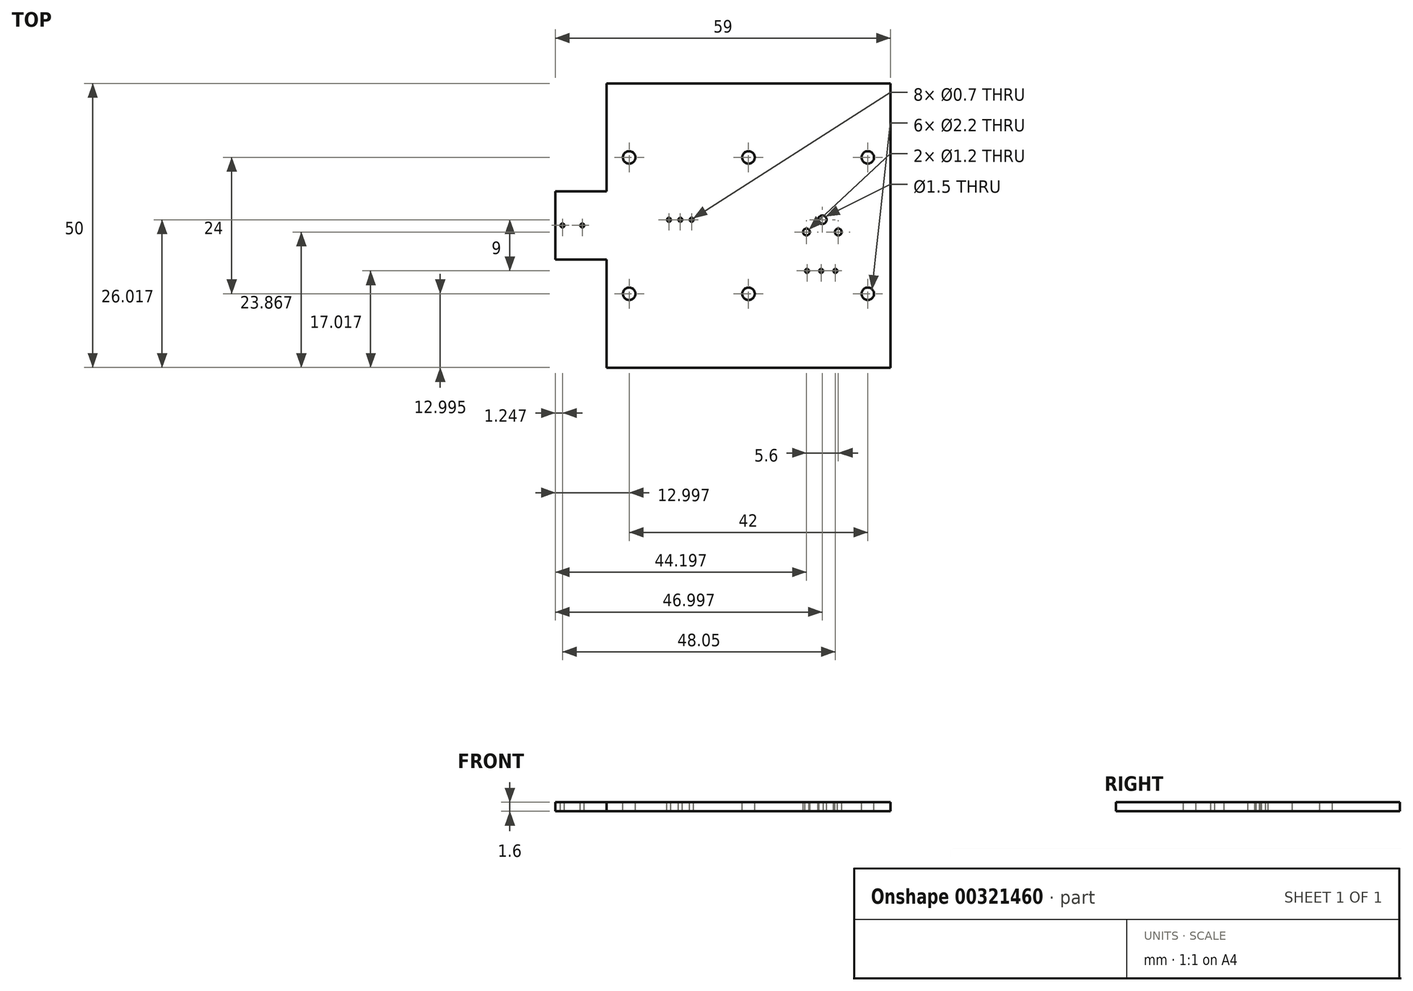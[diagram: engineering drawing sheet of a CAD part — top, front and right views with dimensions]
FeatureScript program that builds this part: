
annotation { "Feature Type Name" : "Feature", "Feature Type Description" : "" }
export const myFeature = defineFeature(function(context is Context, id is Id, definition is map)
    precondition{}
    {
        {
            var Q0;
            Q0=qCreatedBy(makeId("Top.planeOp"),FACE);
            var sketch = newSketch(context, id + "F0", { "sketchPlane" : qUnion([Q0])});
            skLineSegment(sketch, "E0", {"start": v(41.32, 33.18) * mm, "end": v(41.32, -3.82) * mm, "construction": true});
            skLineSegment(sketch, "E1.bottom", {"start": v(7.32, 8.68) * mm, "end": v(66.32, 8.68) * mm});
            skLineSegment(sketch, "E1.top", {"start": v(7.32, 20.68) * mm, "end": v(66.32, 20.68) * mm});
            skLineSegment(sketch, "E1.left", {"start": v(7.32, 8.68) * mm, "end": v(7.32, 20.68) * mm});
            skLineSegment(sketch, "E1.right", {"start": v(75.32, 8.68) * mm, "end": v(75.32, 20.68) * mm, "construction": true});
            skPoint(sketch, "E1.middle", {"position": v(41.32, 14.68) * mm});
            skLineSegment(sketch, "E2.bottom", {"start": v(66.32, 39.68) * mm, "end": v(16.32, 39.68) * mm});
            skLineSegment(sketch, "E2.top", {"start": v(66.32, -10.32) * mm, "end": v(16.32, -10.32) * mm});
            skLineSegment(sketch, "E2.left", {"start": v(66.32, 39.68) * mm, "end": v(66.32, -10.32) * mm});
            skLineSegment(sketch, "E2.right", {"start": v(16.32, 39.68) * mm, "end": v(16.32, -10.32) * mm});
            skSolve(sketch);
        }
        {
            var Q0;
            Q0 = qSketchRegion(id + "F0", true);
            extrude(context, id + "F1", {"entities" : qUnion([Q0]), "depth" : 1.6 * mm});
        }
        {
            var Q0;
            Q0=makeQuery(id+"F1.opExtrude","CAP_FACE",FACE,{"disambiguationData":[OSD([sQuery(id+"F0.wireOp",EDGE,"E1.bottom"),sQuery(id+"F0.wireOp",EDGE,"E1.top"),sQuery(id+"F0.wireOp",EDGE,"E1.left"),sQuery(id+"F0.wireOp",EDGE,"E1.right")])],"isStart":false});
            var sketch = newSketch(context, id + "F2", { "sketchPlane" : qUnion([Q0])});
            skCircle(sketch, "E3", {"center": v(27.32, 15.7) * mm, "radius": 0.35 * mm});
            skLineSegment(sketch, "E4", {"start": v(41.32, 22.32) * mm, "end": v(41.32, 29.29) * mm, "construction": true});
            skCircle(sketch, "E5.1.0.0", {"center": v(29.32, 15.7) * mm, "radius": 0.35 * mm});
            skLineSegment(sketch, "E5.direction1", {"start": v(27.32, 15.7) * mm, "end": v(29.32, 15.7) * mm, "construction": true});
            skCircle(sketch, "E6.0.2.0", {"center": v(31.32, 15.7) * mm, "radius": 0.35 * mm});
            skLineSegment(sketch, "E7", {"start": v(28.32, 15.7) * mm, "end": v(2.32, 15.7) * mm, "construction": true});
            skSolve(sketch);
        }
        {
            var Q0;
            Q0=makeQuery(id+"F1.opExtrude","CAP_FACE",FACE,{"disambiguationData":[OSD([sQuery(id+"F0.wireOp",EDGE,"E1.bottom"),sQuery(id+"F0.wireOp",EDGE,"E1.top"),sQuery(id+"F0.wireOp",EDGE,"E1.left"),sQuery(id+"F0.wireOp",EDGE,"E1.right")])],"isStart":false});
            var sketch = newSketch(context, id + "F3", { "sketchPlane" : qUnion([Q0])});
            skLineSegment(sketch, "E8", {"start": v(54.32, 14.1) * mm, "end": v(54.32, 27.42) * mm, "construction": true});
            skLineSegment(sketch, "E9", {"start": v(41.32, 6.29) * mm, "end": v(41.32, 24.04) * mm, "construction": true});
            skLineSegment(sketch, "E10", {"start": v(51.17, 13.55) * mm, "end": v(51.87, 13.55) * mm, "construction": true});
            skLineSegment(sketch, "E11", {"start": v(51.52, 13.55) * mm, "end": v(51.52, 23.97) * mm, "construction": true});
            skLineSegment(sketch, "E12", {"start": v(53.82, 15.7) * mm, "end": v(54.82, 15.7) * mm, "construction": true});
            skLineSegment(sketch, "E13", {"start": v(54.32, 19.92) * mm, "end": v(54.32, 15.7) * mm, "construction": true});
            skArc(sketch, "E14.0.startCap", {"start": v(53.82, 15.45) * mm, "mid": v(53.57, 15.7) * mm, "end": v(53.82, 15.95) * mm});
            skArc(sketch, "E14.0.endCap", {"start": v(54.82, 15.95) * mm, "mid": v(55.07, 15.7) * mm, "end": v(54.82, 15.45) * mm});
            skLineSegment(sketch, "E14.0.left", {"start": v(53.82, 15.95) * mm, "end": v(54.82, 15.95) * mm});
            skLineSegment(sketch, "E14.0.right", {"start": v(53.82, 15.45) * mm, "end": v(54.82, 15.45) * mm});
            skLineSegment(sketch, "E15", {"start": v(50.5, 14.7) * mm, "end": v(53.65, 14.7) * mm, "construction": true});
            skArc(sketch, "E16.0.startCap", {"start": v(51.87, 13.8) * mm, "mid": v(52.12, 13.55) * mm, "end": v(51.87, 13.3) * mm});
            skArc(sketch, "E16.0.endCap", {"start": v(51.17, 13.3) * mm, "mid": v(50.92, 13.55) * mm, "end": v(51.17, 13.8) * mm});
            skLineSegment(sketch, "E16.0.left", {"start": v(51.17, 13.3) * mm, "end": v(51.87, 13.3) * mm});
            skLineSegment(sketch, "E16.0.right", {"start": v(51.17, 13.8) * mm, "end": v(51.87, 13.8) * mm});
            skArc(sketch, "E17.MirrorCS", {"start": v(57.47, 13.3) * mm, "mid": v(57.72, 13.55) * mm, "end": v(57.47, 13.8) * mm});
            skLineSegment(sketch, "E18.MirrorCS", {"start": v(57.47, 13.3) * mm, "end": v(56.77, 13.3) * mm});
            skLineSegment(sketch, "E19.MirrorCS", {"start": v(57.47, 13.8) * mm, "end": v(56.77, 13.8) * mm});
            skArc(sketch, "E20.MirrorCS", {"start": v(56.77, 13.8) * mm, "mid": v(56.52, 13.55) * mm, "end": v(56.77, 13.3) * mm});
            skLineSegment(sketch, "E21", {"start": v(50.5, 14.7) * mm, "end": v(2.32, 14.7) * mm, "construction": true});
            skCircle(sketch, "E22", {"center": v(51.52, 13.55) * mm, "radius": 0.6 * mm});
            skCircle(sketch, "E23", {"center": v(54.32, 15.7) * mm, "radius": 0.75 * mm});
            skCircle(sketch, "E24", {"center": v(57.12, 13.55) * mm, "radius": 0.6 * mm});
            skPoint(sketch, "E24.centerSnap0", {"position": v(57.12, 13.3) * mm});
            skSolve(sketch);
        }
        {
            var Q0;
            Q0=makeQuery(id+"F1.opExtrude","CAP_FACE",FACE,{"disambiguationData":[OSD([sQuery(id+"F0.wireOp",EDGE,"E1.bottom"),sQuery(id+"F0.wireOp",EDGE,"E1.top"),sQuery(id+"F0.wireOp",EDGE,"E1.left"),sQuery(id+"F0.wireOp",EDGE,"E1.right")])],"isStart":false});
            var sketch = newSketch(context, id + "F4", { "sketchPlane" : qUnion([Q0])});
            skCircle(sketch, "E25", {"center": v(51.62, 6.7) * mm, "radius": 0.35 * mm});
            skCircle(sketch, "E26.1.0.0", {"center": v(56.62, 6.7) * mm, "radius": 0.35 * mm});
            skLineSegment(sketch, "E26.direction1", {"start": v(51.62, 6.7) * mm, "end": v(56.62, 6.7) * mm, "construction": true});
            skLineSegment(sketch, "E27", {"start": v(41.32, 6.29) * mm, "end": v(41.32, 17.65) * mm, "construction": true});
            skLineSegment(sketch, "E28", {"start": v(54.12, 6.7) * mm, "end": v(54.12, 23.7) * mm, "construction": true});
            skCircle(sketch, "E29", {"center": v(54.12, 6.7) * mm, "radius": 0.35 * mm});
            skLineSegment(sketch, "E30", {"start": v(2.32, 14.7) * mm, "end": v(80.32, 14.7) * mm, "construction": true});
            skSolve(sketch);
        }
        {
            var Q0;
            Q0=makeQuery(id+"F1.opExtrude","CAP_FACE",FACE,{"disambiguationData":[OSD([sQuery(id+"F0.wireOp",EDGE,"E1.bottom"),sQuery(id+"F0.wireOp",EDGE,"E1.top"),sQuery(id+"F0.wireOp",EDGE,"E1.left"),sQuery(id+"F0.wireOp",EDGE,"E1.right")])],"isStart":false});
            var sketch = newSketch(context, id + "F5", { "sketchPlane" : qUnion([Q0])});
            skCircle(sketch, "E31", {"center": v(8.57, 14.7) * mm, "radius": 0.35 * mm});
            skCircle(sketch, "E32.1.0.0", {"center": v(12.07, 14.7) * mm, "radius": 0.35 * mm});
            skLineSegment(sketch, "E32.direction1", {"start": v(8.57, 14.7) * mm, "end": v(12.07, 14.7) * mm, "construction": true});
            skLineSegment(sketch, "E33", {"start": v(10.32, 14.7) * mm, "end": v(10.32, 13.4) * mm, "construction": true});
            skLineSegment(sketch, "E34", {"start": v(2.32, 14.7) * mm, "end": v(80.32, 14.7) * mm, "construction": true});
            skSolve(sketch);
        }
        {
            var Q0;
            Q0 = qSketchRegion(id + "F4", true);
            var Q1;
            Q1 = qSketchRegion(id + "FzkBYEW2gLY1UZx_1", true);
            var Q2;
            Q2 = qSketchRegion(id + "F5", true);
            var Q3;
            Q3 = qSketchRegion(id + "F3", true);
            var Q4;
            Q4 = qSketchRegion(id + "F2", true);
            extrude(context, id + "F6", {"entities" : qUnion([Q0, Q1, Q2, Q3, Q4]), "operationType" : NewBodyOperationType.REMOVE, "oppositeDirection" : true, "depth" : 4 * mm});
        }
        {
            var Q0;
            Q0=makeQuery(id+"F1.opExtrude","CAP_FACE",FACE,{"disambiguationData":[OSD([sQuery(id+"F0.wireOp",EDGE,"E1.bottom"),sQuery(id+"F0.wireOp",EDGE,"E1.top"),sQuery(id+"F0.wireOp",EDGE,"E1.left"),sQuery(id+"F0.wireOp",EDGE,"E1.right")])],"isStart":false});
            var sketch = newSketch(context, id + "F7", { "sketchPlane" : qUnion([Q0])});
            skCircle(sketch, "E35", {"center": v(62.32, 26.68) * mm, "radius": 1.1 * mm});
            skCircle(sketch, "E36.MirrorC", {"center": v(20.32, 26.68) * mm, "radius": 1.1 * mm});
            skCircle(sketch, "E37.MirrorC", {"center": v(62.32, 2.68) * mm, "radius": 1.1 * mm});
            skCircle(sketch, "E38.MirrorC", {"center": v(20.32, 2.68) * mm, "radius": 1.1 * mm});
            skCircle(sketch, "E39", {"center": v(41.32, 2.68) * mm, "radius": 1.1 * mm});
            skCircle(sketch, "E40.MirrorC", {"center": v(41.32, 26.68) * mm, "radius": 1.1 * mm});
            skLineSegment(sketch, "E41", {"start": v(41.32, 39.68) * mm, "end": v(41.32, -10.32) * mm, "construction": true});
            skSolve(sketch);
        }
        {
            var Q0;
            Q0 = qSketchRegion(id + "F7", true);
            extrude(context, id + "F8", {"entities" : qUnion([Q0]), "operationType" : NewBodyOperationType.REMOVE, "oppositeDirection" : true, "depth" : 25 * mm});
        }
    });
